# Revit family: ISI_IdealStandard_ShowerMixers_Ceratherm_A4813
name_source: partatom
category: Plumbing Fixtures
revit_build: Autodesk Revit MEP 2012 (Build: 20110309_2315(x64)
units: mm (PartAtom-declared; Revit-internal decimal feet)

## types (1)
- A4813AA-Ceratherm 100 thermostatic exposed shower mixer
    Accessories = www.idealspec.co.uk
    AreaUnits = millimeters
    Assembly Code = C1030200
    AssetType = Fixed
    BIMObjectName = ISI_IdealStandard_ShowerMixers_Ceratherm_A4813
    BREEAMApproved = No
    Brand = Ideal Standard
    CWFU = 0
    Color = Chrome
    ConnectionType = Plumbing
    Cost = 0 $
    Default Elevation = 1000 mm  [stored 3.28084 ft]
    Description = Ceratherm 100 thermostatic exposed shower mixer
    DrainSize = 0 mm  [stored 0 ft]
    DurationUnit = year
    ECA = No
    ExpectedLife = 30
    Features = Thermostatic exposed shower mixer
    Finish = Chrome
    HWFU = 0
    HasTray = No
    IfcExportAs = IfcSanitaryTerminalType
    IfcExportType = SHOWER
    InstallationInstructions = www.idealspec.co.uk/resources.html
    LinearUnits = millimeters
    ManufacturerURL = www.idealspec.co.uk
    Material = Brass
    MaterialThickness = 0 mm  [stored 0 ft]
    Model = A4816AA
    ModelNumber = A4816AA
    ModelReference = Ceratherm 100 thermostatic exposed shower mixer
    NBSDescription = Shower mixers
    NBSReference = 45-35-70/335
    Name = ShowerMixers_Ceratherm-A4816_IdealStandard
    NettWeight = 2.7 Kg
    NominalDepth = 102 mm
    NominalHeight = 56 mm
    NominalLength = 102 mm
    NominalWidth = 310 mm
    Shape = Cylindrical
    ShowerType = Other
    Size = 310 x 102 x 56 mm
    Space = Internal
    SpareParts = www.fastpart-spares.co.uk
    TestPressure = 10 Bar
    URL = www.idealspec.co.uk
    Uniclass2 = Pr_40_20_87_81
    Version = 2
    VolumeUnits = Litres
    WFU = 0
    WRAS = Yes
    WarrantyDescription = Manufacturers Warranty
    WarrantyDurationParts = 5
    WarrantyDurationUnit = year
    WaterEfficientProduct = No

note: [stored X ft] marks values corroborated as IEEE doubles in the binary element streams (Revit-internal decimal feet)

## geometry (parser evidence)
native form markers: Sweep x3
no freeform markers — native parametric forms only
